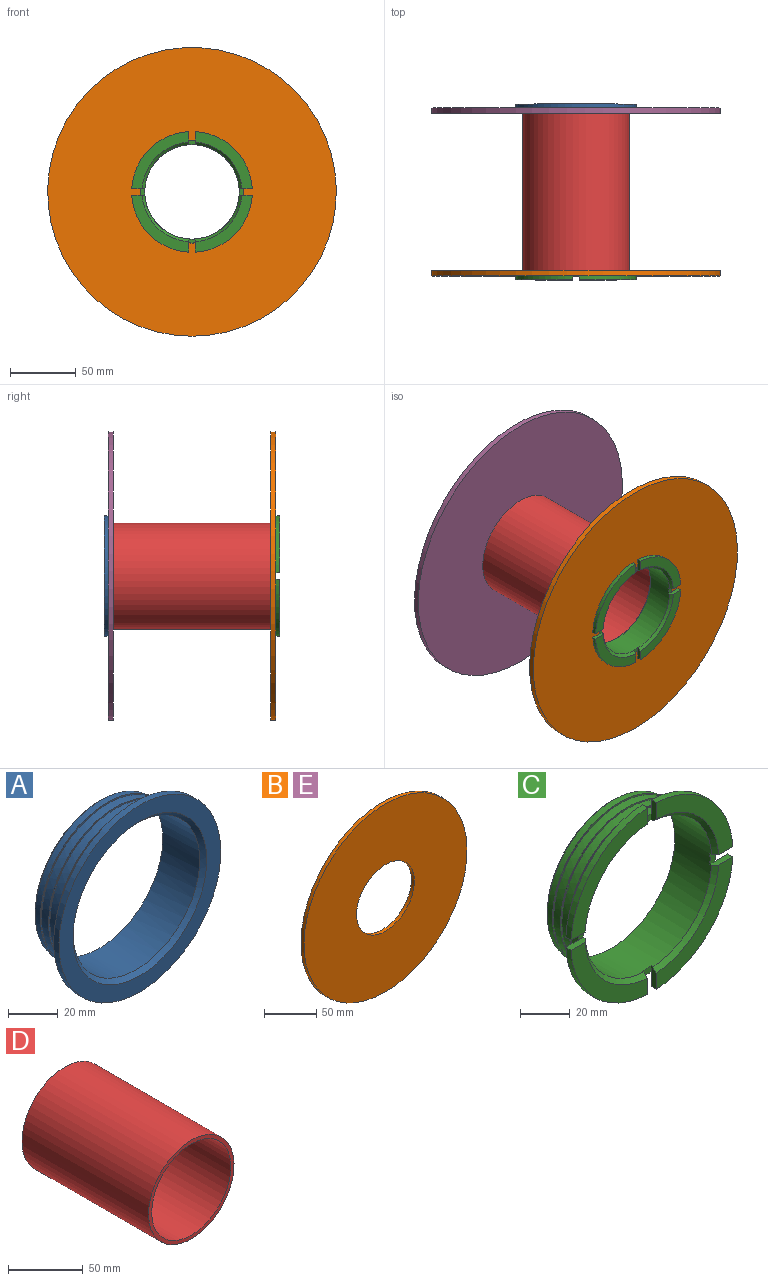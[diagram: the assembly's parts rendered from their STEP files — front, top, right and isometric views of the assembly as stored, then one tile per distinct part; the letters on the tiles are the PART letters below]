
ASSEMBLY  parts=5 mates=8
PART A: 19 faces, bbox 92x23x92 mm
  f0: cylinder r=37.5mm len=75mm, axis (0,-1,0), area 942.5mm2, adj f2,f5
  f1: cylinder r=37.5mm len=75mm, axis (0,-1,0), area 483mm2, adj f3,f16
  f2: cone r=37.5mm half-angle=45deg, axis (0,-1,0), area 218.5mm2, adj f0,f3
  f3: plane 76.3x76.3mm, normal (0,-1,0), area 154.5mm2, adj f1,f2
  f4: cone r=37.5mm half-angle=45deg, axis (0,-1,0), area 218.5mm2, adj f5,f7
  f5: plane 76.3x76.3mm, normal (0,-1,0), area 154.5mm2, adj f0,f4
  f6: cylinder r=37.5mm len=75mm, axis (0,-1,0), area 706.9mm2, adj f13,f18
  f7: cylinder r=37.5mm len=75mm, axis (0,-1,0), area 942.5mm2, adj f4,f14
  f8: cylinder r=46mm len=92mm, axis (0,1,0), area 867.1mm2, adj f9,f10
  f9: plane 92x92mm, normal (0,-1,0), area 2111.2mm2, adj f8,f17
  f10: plane 92x92mm, normal (0,1,0), area 1869.2mm2, adj f8,f15
  f11: cylinder r=36mm len=72mm, axis (0,1,0), area 4750.1mm2, adj f12,f17
  f12: plane 73x73mm, normal (0,1,0), area 113.9mm2, adj f11,f18
  f13: cone r=37.5mm half-angle=45deg, axis (0,-1,0), area 218.5mm2, adj f6,f14
  f14: plane 76.3x76.3mm, normal (0,-1,0), area 154.5mm2, adj f7,f13
  f15: cylinder r=39mm len=78mm, axis (0,-1,0), area 980.2mm2, adj f10,f16
  f16: plane 78x78mm, normal (0,1,0), area 360.5mm2, adj f1,f15
  f17: cone r=36mm half-angle=45deg, axis (0,-1,0), area 657.5mm2, adj f9,f11
  f18: cone r=36.5mm half-angle=45deg, axis (0,-1,0), area 328.8mm2, adj f6,f12
PART B: 4 faces, bbox 220x4x220 mm
  f0: cylinder r=39mm len=78mm, axis (0,1,0), area 980.2mm2, adj f2,f3
  f1: cylinder r=110mm len=220mm, axis (0,1,0), area 2764.6mm2, adj f2,f3
  f2: plane 220x220mm, normal (0,-1,0), area 33234.9mm2, adj f0,f1
  f3: plane 220x220mm, normal (0,1,0), area 33234.9mm2, adj f0,f1
PART C: 43 faces, bbox 91.9x23x91.9 mm
  f0: plane 43.43x43.43mm, normal (0,1,0), area 432.3mm2, adj f5,f21,f37,f40
  f1: cone r=36mm half-angle=45deg, axis (0,-1,0), area 150.2mm2, adj f5,f22,f33,f40
  f2: cylinder r=46mm len=43.43mm, axis (0,1,0), area 201.8mm2, adj f3,f6,f7,f12
  f3: plane 43.43x43.43mm, normal (0,-1,0), area 487.8mm2, adj f2,f6,f8,f12
  f4: plane 5x3.09mm, normal (0,-1,0), area 15mm2, adj f5,f6,f33,f37
  f5: plane 10.02x3mm, normal (0,0,-1), area 28.1mm2, adj f0,f1,f4,f21,f22,f33
  f6: plane 10.02x3mm, normal (0,0,1), area 28.1mm2, adj f2,f3,f4,f7,f8,f33
  f7: plane 43.43x43.43mm, normal (0,1,0), area 432.3mm2, adj f2,f6,f12,f37
  f8: cone r=36mm half-angle=45deg, axis (0,-1,0), area 150.2mm2, adj f3,f6,f12,f33
  f9: cylinder r=46mm len=43.43mm, axis (0,1,0), area 201.8mm2, adj f10,f13,f14,f19
  f10: plane 43.43x43.43mm, normal (0,-1,0), area 487.8mm2, adj f9,f13,f15,f19
  f11: plane 5x3.09mm, normal (0,-1,0), area 15mm2, adj f12,f13,f33,f37
  f12: plane 10.02x3mm, normal (1,0,0), area 28.1mm2, adj f2,f3,f7,f8,f11,f33
  f13: plane 10.02x3mm, normal (-1,0,0), area 28.1mm2, adj f9,f10,f11,f14,f15,f33
  f14: plane 43.43x43.43mm, normal (0,1,0), area 432.3mm2, adj f9,f13,f19,f37
  f15: cone r=36mm half-angle=45deg, axis (0,-1,0), area 150.2mm2, adj f10,f13,f19,f33
  f16: cylinder r=46mm len=43.43mm, axis (0,1,0), area 201.8mm2, adj f17,f20,f23,f41
  f17: plane 43.43x43.43mm, normal (0,-1,0), area 487.8mm2, adj f16,f20,f24,f41
  f18: plane 5x3.09mm, normal (0,-1,0), area 15mm2, adj f19,f20,f33,f37
  f19: plane 10.02x3mm, normal (0,0,1), area 28.1mm2, adj f9,f10,f14,f15,f18,f33
  f20: plane 10.02x3mm, normal (0,0,-1), area 28.1mm2, adj f16,f17,f18,f23,f24,f33
  f21: cylinder r=46mm len=43.43mm, axis (0,1,0), area 201.8mm2, adj f0,f5,f22,f40
  f22: plane 43.43x43.43mm, normal (0,-1,0), area 487.8mm2, adj f1,f5,f21,f40
  f23: plane 43.43x43.43mm, normal (0,1,0), area 432.3mm2, adj f16,f20,f37,f41
  f24: cone r=36mm half-angle=45deg, axis (0,-1,0), area 150.2mm2, adj f17,f20,f33,f41
  f25: cylinder r=37.5mm len=75mm, axis (0,-1,0), area 942.5mm2, adj f27,f30
  f26: cylinder r=37.5mm len=75mm, axis (0,-1,0), area 483mm2, adj f28,f38
  f27: cone r=37.5mm half-angle=45deg, axis (0,-1,0), area 218.5mm2, adj f25,f28
  f28: plane 76.3x76.3mm, normal (0,-1,0), area 154.5mm2, adj f26,f27
  f29: cone r=37.5mm half-angle=45deg, axis (0,-1,0), area 218.5mm2, adj f30,f32
  f30: plane 76.3x76.3mm, normal (0,-1,0), area 154.5mm2, adj f25,f29
  f31: cylinder r=37.5mm len=75mm, axis (0,-1,0), area 706.9mm2, adj f35,f42
  f32: cylinder r=37.5mm len=75mm, axis (0,-1,0), area 942.5mm2, adj f29,f36
  f33: cylinder r=36mm len=72mm, axis (0,1,0), area 4730.1mm2, adj f1,f4,f5,f6,f8,f11,f12,f13
  f34: plane 73x73mm, normal (0,1,0), area 113.9mm2, adj f33,f42
  f35: cone r=37.5mm half-angle=45deg, axis (0,-1,0), area 218.5mm2, adj f31,f36
  f36: plane 76.3x76.3mm, normal (0,-1,0), area 154.5mm2, adj f32,f35
  f37: cylinder r=39mm len=78mm, axis (0,-1,0), area 980.2mm2, adj f0,f4,f7,f11,f14,f18,f23,f38
  f38: plane 78x78mm, normal (0,1,0), area 360.5mm2, adj f26,f37
  f39: plane 5x3.09mm, normal (0,-1,0), area 15mm2, adj f33,f37,f40,f41
  f40: plane 10.02x3mm, normal (1,0,0), area 28.1mm2, adj f0,f1,f21,f22,f33,f39
  f41: plane 10.02x3mm, normal (-1,0,0), area 28.1mm2, adj f16,f17,f23,f24,f33,f39
  f42: cone r=36.5mm half-angle=45deg, axis (0,-1,0), area 328.8mm2, adj f31,f34
PART D: 4 faces, bbox 81x120x81 mm
  f0: cylinder r=37.5mm len=120mm, axis (0,1,0), area 28274.3mm2, adj f2,f3
  f1: cylinder r=40.5mm len=120mm, axis (0,1,0), area 30536.3mm2, adj f2,f3
  f2: plane 81x81mm, normal (0,1,0), area 735.1mm2, adj f0,f1
  f3: plane 81x81mm, normal (0,-1,0), area 735.1mm2, adj f0,f1
PART E: same geometry as B
PLACE A rot(axis=(0,0,1),180deg) t=(104.46,9.72,-261.21)mm
PLACE B t=(104.46,-110.28,-261.21)mm
PLACE C t=(104.46,-110.28,-261.21)mm
PLACE D t=(104.46,9.72,-261.21)mm
PLACE E t=(104.46,13.72,-261.21)mm
MATE cylindrical E.f1 <-> D.f1  axis (0,-1,0) through (104.46,9.72,-261.21)mm
MATE planar B.f1 <-> C.f23  axis (0,-1,0) through (104.46,-114.28,-261.21)mm
MATE cylindrical D.f1 <-> B.f1  axis (0,-1,0) through (104.46,-110.28,-261.21)mm
MATE cylindrical C.f25 <-> B.f0  axis (0,1,0) through (104.46,-94.28,-261.21)mm
MATE cylindrical D.f1 <-> B.f1  axis (0,-1,0) through (104.46,-110.28,-261.21)mm
MATE cylindrical A.f11 <-> E.f1  axis (0,-1,0) through (104.46,13.72,-261.21)mm
MATE cylindrical A.f8 <-> E.f0  axis (0,-1,0) through (104.46,13.72,-261.21)mm
MATE cylindrical A.f8 <-> D.f1  axis (0,-1,0) through (104.46,13.72,-261.21)mm
